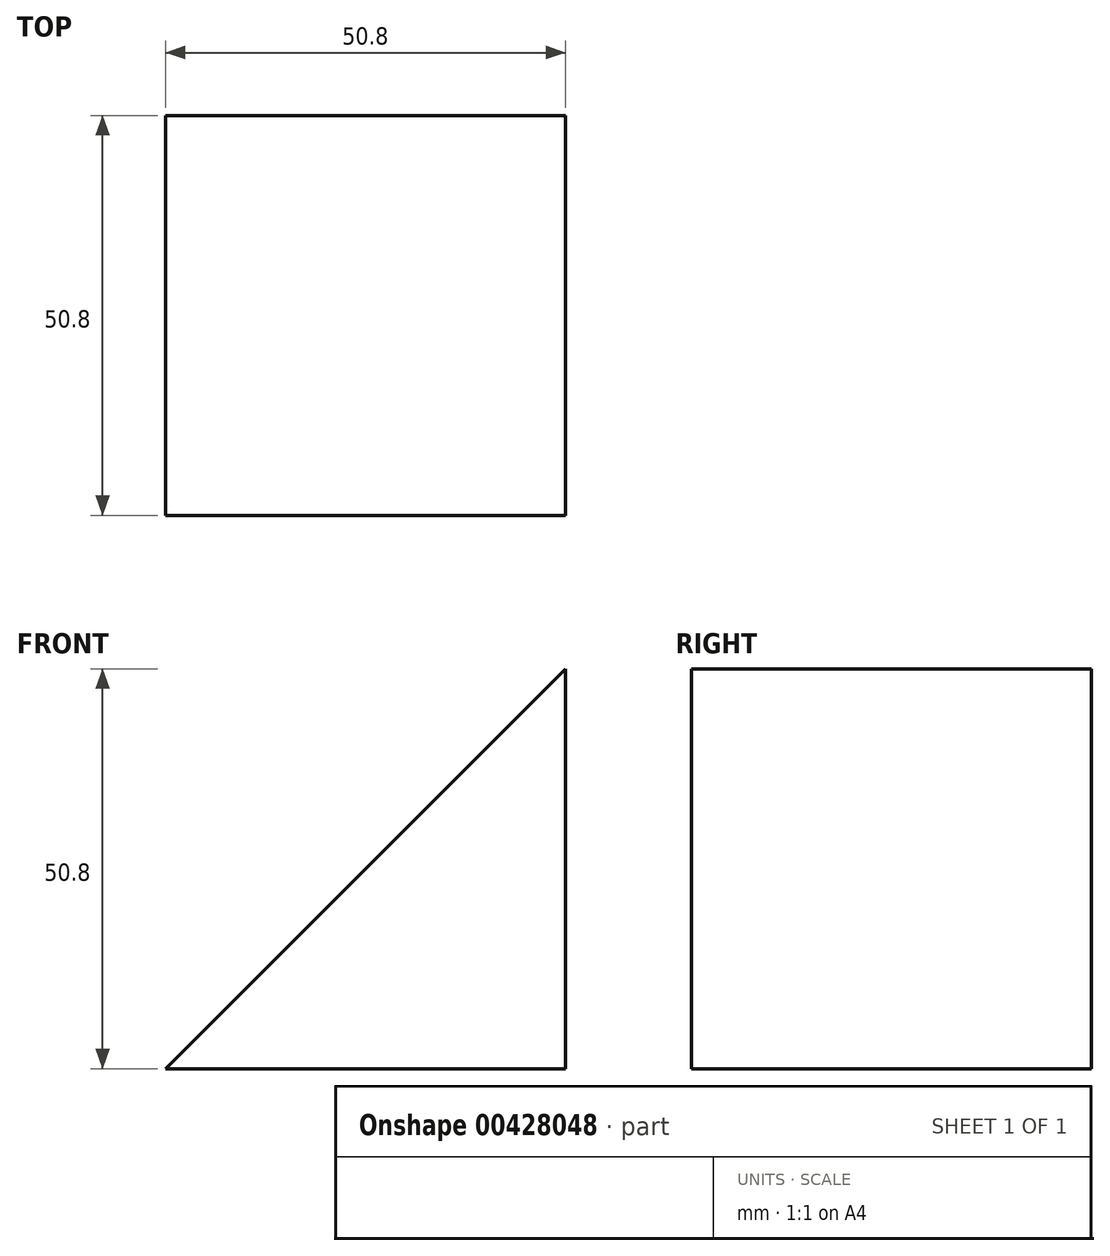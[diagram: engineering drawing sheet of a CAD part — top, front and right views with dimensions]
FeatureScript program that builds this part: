
annotation { "Feature Type Name" : "Feature", "Feature Type Description" : "" }
export const myFeature = defineFeature(function(context is Context, id is Id, definition is map)
    precondition{}
    {
        {
            var Q0;
            Q0=qCreatedBy(makeId("Front.planeOp"),FACE);
            var sketch = newSketch(context, id + "F0", { "sketchPlane" : qUnion([Q0])});
            skLineSegment(sketch, "E0", {"start": v(0, 0) * mm, "end": v(0, 50.8) * mm});
            skLineSegment(sketch, "E1", {"start": v(0, 0) * mm, "end": v(-50.8, 0) * mm});
            skLineSegment(sketch, "E2", {"start": v(-50.8, 0) * mm, "end": v(0, 50.8) * mm});
            skSolve(sketch);
        }
        {
            var Q0;
            Q0=makeQuery(id+"F0.imprint","IMPRINT",FACE,{"disambiguationData":[TD([[makeQuery(id+"F0.imprint","IMPRINT",EDGE,{"derivedFrom":sQuery(id+"F0.wireOp",EDGE,"E0")}),1.0]])]});
            extrude(context, id + "F1", {"entities" : qUnion([Q0]), "depth" : 50.8 * mm});
        }
    });
